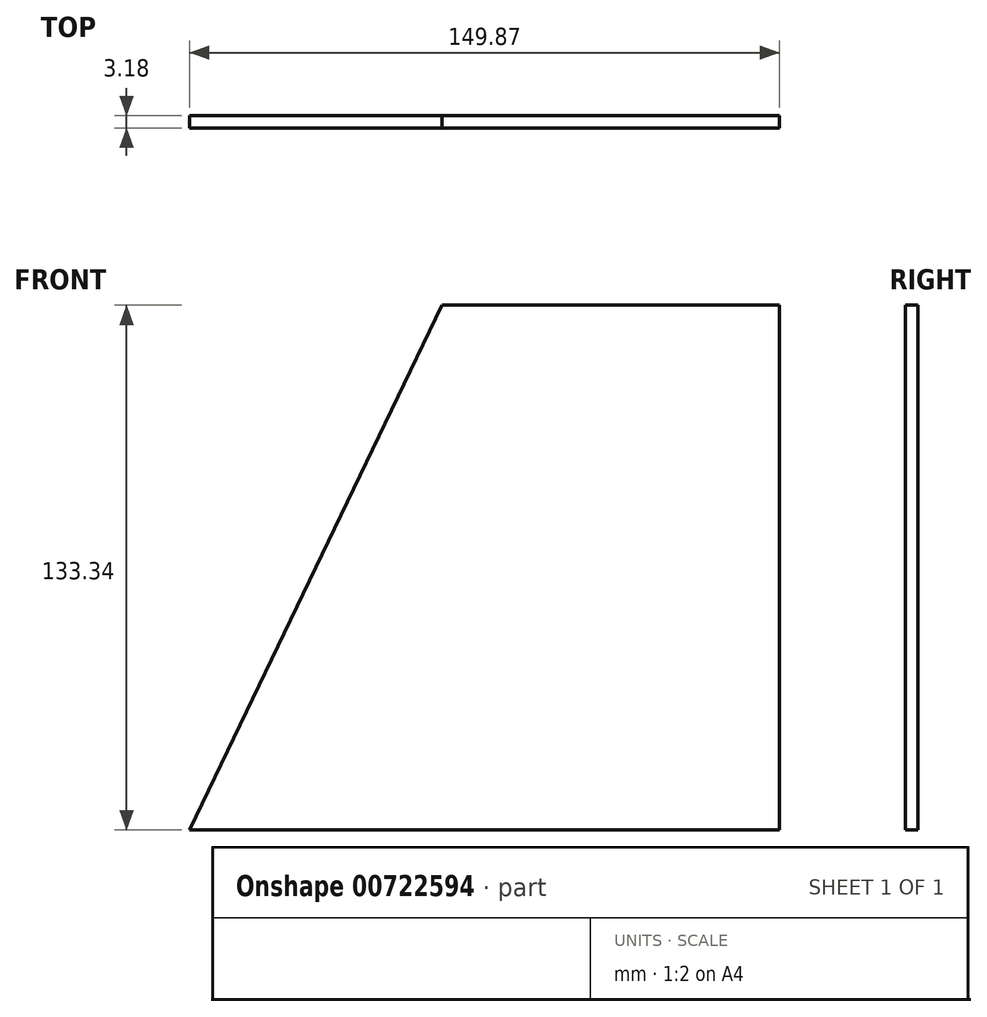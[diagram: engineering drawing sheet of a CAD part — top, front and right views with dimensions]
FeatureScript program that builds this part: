
annotation { "Feature Type Name" : "Feature", "Feature Type Description" : "" }
export const myFeature = defineFeature(function(context is Context, id is Id, definition is map)
    precondition{}
    {
        {
            var Q0;
            Q0=qCreatedBy(makeId("Front.planeOp"),FACE);
            var sketch = newSketch(context, id + "F0", { "sketchPlane" : qUnion([Q0])});
            skLineSegment(sketch, "E0.bottom", {"start": v(-82.55, -66.68) * mm, "end": v(82.55, -66.68) * mm});
            skLineSegment(sketch, "E0.top", {"start": v(-82.55, 66.68) * mm, "end": v(82.55, 66.68) * mm});
            skLineSegment(sketch, "E0.left", {"start": v(-82.55, -66.68) * mm, "end": v(-82.55, 66.68) * mm});
            skLineSegment(sketch, "E0.right", {"start": v(82.55, -66.68) * mm, "end": v(82.55, 66.68) * mm});
            skPoint(sketch, "E0.middle", {"position": v(0, 0) * mm});
            skSolve(sketch);
        }
        {
            var Q0;
            Q0=makeQuery(id+"F0.imprint","IMPRINT",FACE,{"disambiguationData":[TD([[makeQuery(id+"F0.imprint","IMPRINT",EDGE,{"derivedFrom":sQuery(id+"F0.wireOp",EDGE,"E0.bottom")}),1.0]])]});
            extrude(context, id + "F1", {"entities" : qUnion([Q0]), "endBound" : BoundingType.SYMMETRIC, "depth" : 3.17 * mm, "offsetDistance" : 25 * mm});
        }
        {
            var Q0;
            Q0=makeQuery(id+"F1.opExtrude","SWEPT_EDGE",EDGE,{"disambiguationData":[OSD([sQuery(id+"F0.wireOp",EDGE,"E0.top"),sQuery(id+"F0.wireOp",EDGE,"E0.left")])]});
            chamfer(context, id + "F2", {"entities" : qUnion([Q0]), "chamferType" : ChamferType.TWO_OFFSETS, "width1" : 165 * mm, "oppositeDirection" : false, "width2" : 79.38 * mm, "tangentPropagation" : true});
        }
    });
